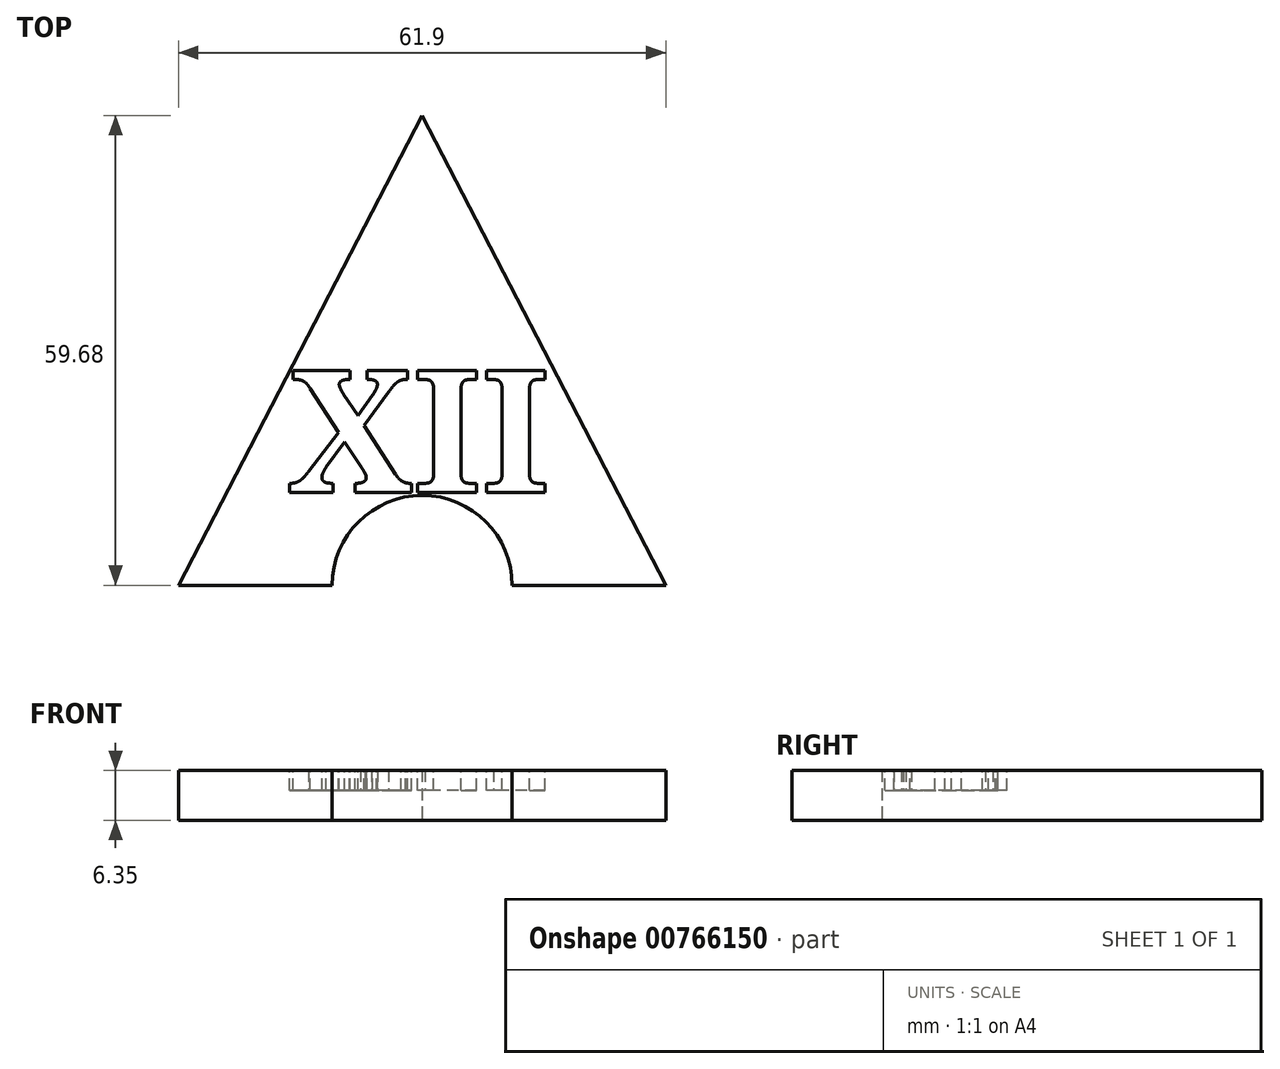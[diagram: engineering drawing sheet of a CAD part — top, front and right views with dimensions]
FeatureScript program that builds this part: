
annotation { "Feature Type Name" : "Feature", "Feature Type Description" : "" }
export const myFeature = defineFeature(function(context is Context, id is Id, definition is map)
    precondition{}
    {
        {
            var Q0;
            Q0=qCreatedBy(makeId("Top.planeOp"),FACE);
            var sketch = newSketch(context, id + "F0", { "sketchPlane" : qUnion([Q0])});
            skCircle(sketch, "E0.cCircle", {"center": v(0, -0.3) * mm, "radius": 17.87 * mm, "construction": true});
            skLineSegment(sketch, "E0.0", {"start": v(30.95, -18.16) * mm, "end": v(-30.95, -18.16) * mm});
            skLineSegment(sketch, "E0.1", {"start": v(-30.95, -18.16) * mm, "end": v(0, 41.52) * mm});
            skLineSegment(sketch, "E0.2", {"start": v(0, 41.52) * mm, "end": v(30.95, -18.16) * mm});
            skPoint(sketch, "E0.0.midPoint", {"position": v(0, -18.16) * mm});
            skSolve(sketch);
        }
        {
            var Q0;
            Q0=makeQuery(id+"F0.imprint","IMPRINT",FACE,{"disambiguationData":[TD([[makeQuery(id+"F0.imprint","IMPRINT",EDGE,{"derivedFrom":sQuery(id+"F0.wireOp",EDGE,"E0.0")}),-1.0]])]});
            extrude(context, id + "F1", {"entities" : qUnion([Q0]), "depth" : 6.35 * mm, "offsetDistance" : 25.4 * mm});
        }
        {
            var Q0;
            Q0=sQuery(id+"F0.wireOp",VERTEX,"E0.0.midPoint");
            var Q1;
            Q1=makeQuery(id+"F1.opExtrude","SWEPT_BODY",BODY,{"disambiguationData":[OSD([sQuery(id+"F0.wireOp",EDGE,"E0.0"),sQuery(id+"F0.wireOp",EDGE,"E0.1"),sQuery(id+"F0.wireOp",EDGE,"E0.2")])]});
            hole(context, id + "F2", {"style" : HoleStyle.SIMPLE, "endStyle" : HoleEndStyle.THROUGH, "oppositeDirection" : true, "holeDiameter" : 22.86 * mm, "majorDiameter" : 6.35 * mm, "isTappedThrough" : true, "tappedDepth" : 12.7 * mm, "tapClearance" : 3, "locations" : qUnion([Q0]), "scope" : qUnion([Q1])});
        }
        {
            var Q0;
            Q0=makeQuery(id+"F1.opExtrude","CAP_FACE",FACE,{"disambiguationData":[OSD([sQuery(id+"F0.wireOp",EDGE,"E0.0"),sQuery(id+"F0.wireOp",EDGE,"E0.1"),sQuery(id+"F0.wireOp",EDGE,"E0.2")])],"isStart":false});
            var sketch = newSketch(context, id + "F3", { "sketchPlane" : qUnion([Q0])});
            skText(sketch, "E1", { "text": "XII", "fontName": "NotoSerif-Bold.ttf"});
            const initialGuessF3  = {"E1": [-0.01704, -0.00635, 1, 0, 0.01562]};
            skSetInitialGuess(sketch, initialGuessF3);
            skSolve(sketch);
        }
        {
            var Q0;
            Q0 = qSketchRegion(id + "F3", true);
            extrude(context, id + "F4", {"entities" : qUnion([Q0]), "operationType" : NewBodyOperationType.REMOVE, "oppositeDirection" : true, "depth" : 2.54 * mm, "offsetDistance" : 25.4 * mm});
        }
    });
